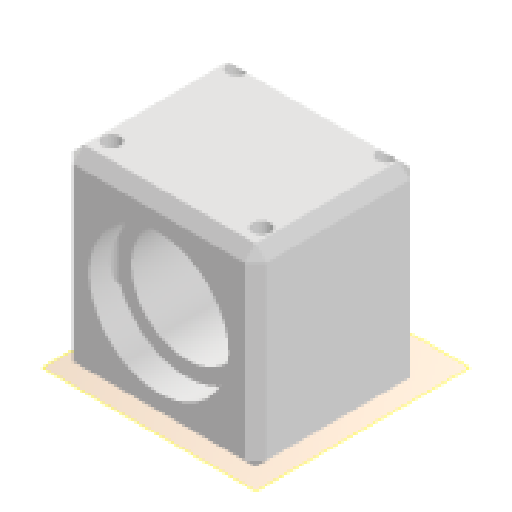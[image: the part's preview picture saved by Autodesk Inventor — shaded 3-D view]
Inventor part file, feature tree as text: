
AUTODESK INVENTOR PART (.ipt)
format: ipt  version: 2024.1 (Build 281209000, 209)  size: 169,984 bytes
history: native  units: mm
features: extrude x3, sketch x3, reference x3, other x3, plane x1, chamfer x1, mirror x1
ambient origin geometry x8: Origin, YZ Plane, XZ Plane, XY Plane, X Axis, Y Axis, Z Axis, Center Point
bodies: Volumenkörper1 (feature_tree)
feature tree (15):
  plane  "Arbeitsebene1"
  extrude  "Extrusion1"  Depth=34.8mm
  extrude  "Extrusion2"  Depth=17.4mm TaperAngle=0.0deg
  extrude  "Extrusion3"  Depth=5.0mm TaperAngle=0.0deg
  chamfer  "Fasen1"  Distance=20.0mm
  mirror  "Spiegeln1"
  sketch  "Skizze1"  dims[d0=34.8mm d1=30.0mm]
  reference  "Referenz1"
  sketch  "Skizze2"  dims[d2=2.3mm d3=17.4mm d4=0.0mm]
  reference  "Referenz2"
  sketch  "Skizze3"  dims[d5=25.0mm d6=5.0mm d7=0.0mm d8=20.0mm d9=0.0mm d10=0.0mm d11=2.0mm d12=2.0mm d13=45.0deg]
  reference  "Referenz3"
  other  "Assembly_MicroscopeInABox_v0.iam"
  other  "MIAB_Case_v0:1"
  other  "00_10x_Objective_ViewSolutions_bm05073332:1"
